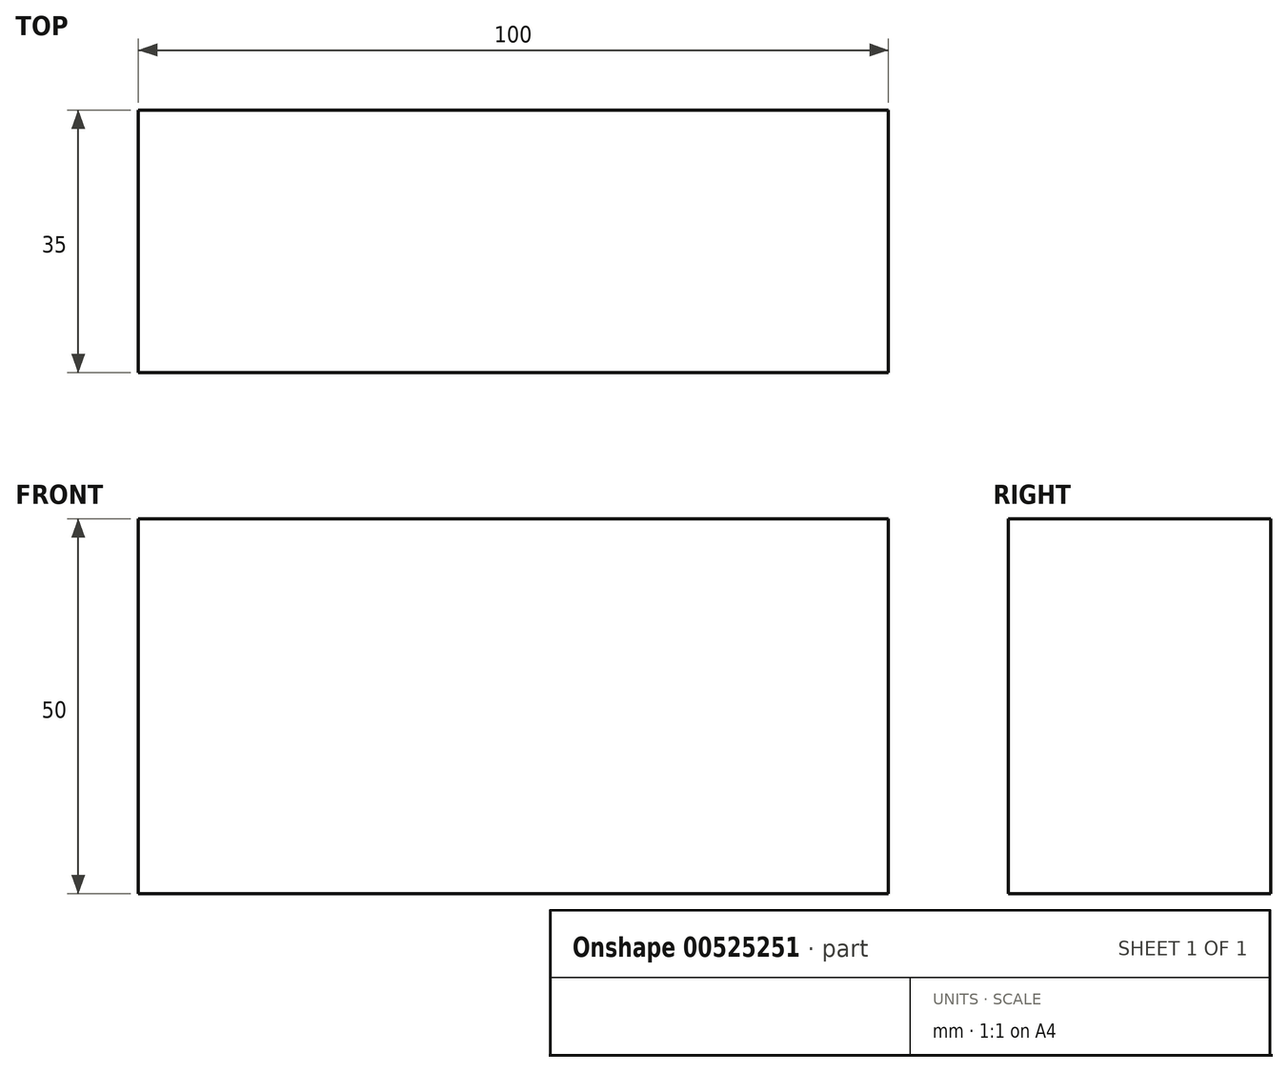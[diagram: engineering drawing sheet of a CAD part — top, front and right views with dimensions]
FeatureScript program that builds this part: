
annotation { "Feature Type Name" : "Feature", "Feature Type Description" : "" }
export const myFeature = defineFeature(function(context is Context, id is Id, definition is map)
    precondition{}
    {
        {
            var Q0;
            Q0=qCreatedBy(makeId("Front.planeOp"),FACE);
            var sketch = newSketch(context, id + "F0", { "sketchPlane" : qUnion([Q0])});
            skLineSegment(sketch, "E0.bottom", {"start": v(-86.64, 43.25) * mm, "end": v(13.36, 43.25) * mm});
            skLineSegment(sketch, "E0.top", {"start": v(-86.64, -6.75) * mm, "end": v(13.36, -6.75) * mm});
            skLineSegment(sketch, "E0.left", {"start": v(-86.64, 43.25) * mm, "end": v(-86.64, -6.75) * mm});
            skLineSegment(sketch, "E0.right", {"start": v(13.36, 43.25) * mm, "end": v(13.36, -6.75) * mm});
            skSolve(sketch);
        }
        {
            var Q0;
            Q0=makeQuery(id+"F0.imprint","IMPRINT",FACE,{"disambiguationData":[TD([[makeQuery(id+"F0.imprint","IMPRINT",EDGE,{"derivedFrom":sQuery(id+"F0.wireOp",EDGE,"E0.bottom")}),-1.0]])]});
            extrude(context, id + "F1", {"entities" : qUnion([Q0]), "depth" : 35 * mm, "offsetDistance" : 25 * mm});
        }
    });
